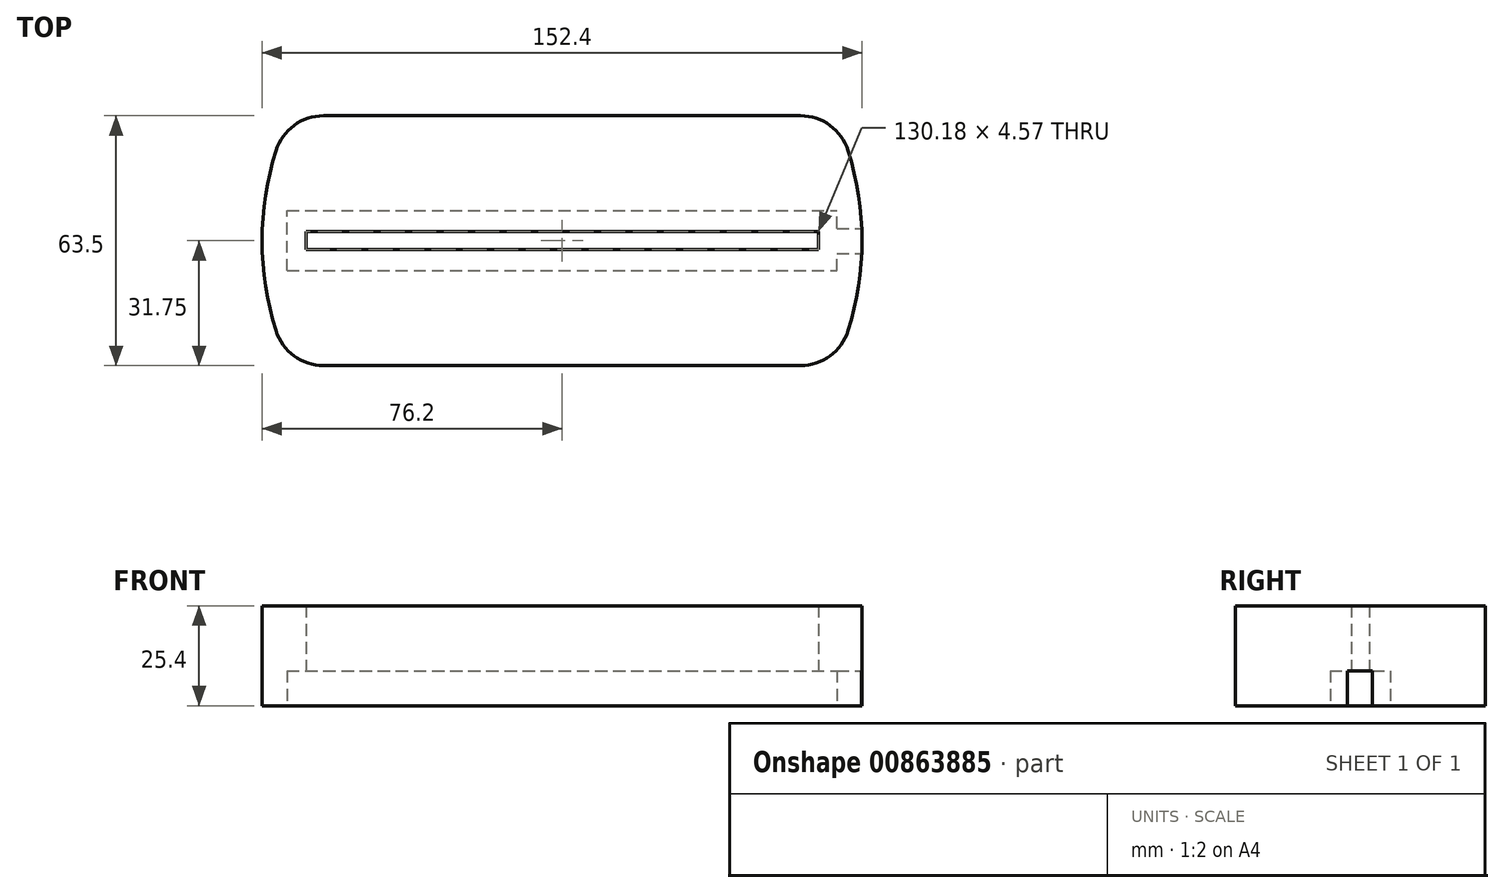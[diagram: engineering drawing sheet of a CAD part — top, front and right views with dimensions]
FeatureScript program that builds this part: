
annotation { "Feature Type Name" : "Feature", "Feature Type Description" : "" }
export const myFeature = defineFeature(function(context is Context, id is Id, definition is map)
    precondition{}
    {
        {
            var Q0;
            Q0=qCreatedBy(makeId("Top.planeOp"),FACE);
            var sketch = newSketch(context, id + "F0", { "sketchPlane" : qUnion([Q0])});
            skArc(sketch, "E0", {"start": v(-69.27, 31.75) * mm, "mid": v(-76.2, 0) * mm, "end": v(-69.27, -31.75) * mm});
            skLineSegment(sketch, "E1", {"start": v(-69.27, 31.75) * mm, "end": v(69.27, 31.75) * mm});
            skLineSegment(sketch, "E2.MirrorCS", {"start": v(-69.27, -31.75) * mm, "end": v(69.27, -31.75) * mm});
            skArc(sketch, "E3.trimOffspring", {"start": v(69.27, -31.75) * mm, "mid": v(76.2, 0) * mm, "end": v(69.27, 31.75) * mm});
            skSolve(sketch);
        }
        {
            var Q0;
            Q0=makeQuery(id+"F0.imprint","IMPRINT",FACE,{"disambiguationData":[TD([[makeQuery(id+"F0.imprint","IMPRINT",EDGE,{"derivedFrom":sQuery(id+"F0.wireOp",EDGE,"E0")}),1.0]])]});
            extrude(context, id + "F1", {"entities" : qUnion([Q0]), "depth" : 25.4 * mm, "offsetDistance" : 25.4 * mm});
        }
        {
            var Q0;
            Q0=makeQuery(id+"F1.opExtrude","CAP_FACE",FACE,{"disambiguationData":[OSD([sQuery(id+"F0.wireOp",EDGE,"E0"),sQuery(id+"F0.wireOp",EDGE,"E1"),sQuery(id+"F0.wireOp",EDGE,"E2.MirrorCS"),sQuery(id+"F0.wireOp",EDGE,"E3.trimOffspring")])],"isStart":true});
            var sketch = newSketch(context, id + "F2", { "sketchPlane" : qUnion([Q0])});
            skLineSegment(sketch, "E4.MirrorCS", {"start": v(-179.86, 3.34) * mm, "end": v(-179.86, -2.97) * mm});
            skLineSegment(sketch, "E5.bottom", {"start": v(-65.09, 2.29) * mm, "end": v(65.09, 2.29) * mm});
            skLineSegment(sketch, "E5.top", {"start": v(-65.09, -2.29) * mm, "end": v(65.09, -2.29) * mm});
            skLineSegment(sketch, "E5.left", {"start": v(-65.09, 2.29) * mm, "end": v(-65.09, -2.29) * mm});
            skLineSegment(sketch, "E5.right", {"start": v(65.09, 2.29) * mm, "end": v(65.09, -2.29) * mm});
            skPoint(sketch, "E5.middle", {"position": v(0, 0) * mm});
            skSolve(sketch);
        }
        {
            var Q0;
            Q0=makeQuery(id+"F2.imprint","IMPRINT",FACE,{"disambiguationData":[TD([[makeQuery(id+"F2.imprint","IMPRINT",EDGE,{"derivedFrom":sQuery(id+"F2.wireOp",EDGE,"E5.bottom")}),-1.0]])]});
            extrude(context, id + "F3", {"entities" : qUnion([Q0]), "operationType" : NewBodyOperationType.REMOVE, "endBound" : BoundingType.THROUGH_ALL, "oppositeDirection" : true, "depth" : 25.4 * mm, "offsetDistance" : 25.4 * mm});
        }
        {
            var Q0;
            Q0=makeQuery(id+"F1.opExtrude","CAP_FACE",FACE,{"disambiguationData":[OSD([sQuery(id+"F0.wireOp",EDGE,"E0"),sQuery(id+"F0.wireOp",EDGE,"E1"),sQuery(id+"F0.wireOp",EDGE,"E2.MirrorCS"),sQuery(id+"F0.wireOp",EDGE,"E3.trimOffspring")])],"isStart":true});
            var sketch = newSketch(context, id + "F4", { "sketchPlane" : qUnion([Q0])});
            skLineSegment(sketch, "E6.bottom", {"start": v(-69.85, 7.62) * mm, "end": v(69.85, 7.62) * mm});
            skLineSegment(sketch, "E6.top", {"start": v(-69.85, -7.62) * mm, "end": v(69.85, -7.62) * mm});
            skLineSegment(sketch, "E6.left", {"start": v(-69.85, 7.62) * mm, "end": v(-69.85, -7.62) * mm});
            skLineSegment(sketch, "E6.right", {"start": v(69.85, 7.62) * mm, "end": v(69.85, -7.62) * mm});
            skPoint(sketch, "E6.middle", {"position": v(0, 0) * mm});
            skLineSegment(sketch, "E7", {"start": v(69.85, 3.23) * mm, "end": v(76.13, 3.23) * mm});
            skLineSegment(sketch, "E8", {"start": v(69.85, -3.12) * mm, "end": v(76.14, -3.12) * mm});
            skArc(sketch, "E9", {"start": v(76.14, -3.12) * mm, "mid": v(76.2, 0.06) * mm, "end": v(76.13, 3.23) * mm});
            skSolve(sketch);
        }
        {
            var Q0;
            Q0=makeQuery(id+"F4.imprint","IMPRINT",FACE,{"disambiguationData":[TD([[makeQuery(id+"F4.imprint","IMPRINT",EDGE,{"derivedFrom":sQuery(id+"F4.wireOp",EDGE,"E6.bottom")}),-1.0]])]});
            var Q1;
            {var subQ0=sQuery(id+"F4.wireOp",EDGE,"E7");Q1=makeQuery(id+"F4.imprint","IMPRINT",FACE,{"disambiguationData":[TD([[makeQuery(id+"F4.imprint","IMPRINT",EDGE,{"derivedFrom":subQ0}),-1.0]])]});}
            extrude(context, id + "F5", {"entities" : qUnion([Q0, Q1]), "operationType" : NewBodyOperationType.REMOVE, "oppositeDirection" : true, "depth" : 8.9 * mm, "offsetDistance" : 25.4 * mm});
        }
        {
            var Q0;
            Q0=makeQuery(id+"F1.opExtrude","SWEPT_EDGE",EDGE,{"disambiguationData":[OSD([sQuery(id+"F0.wireOp",EDGE,"E2.MirrorCS"),sQuery(id+"F0.wireOp",EDGE,"E3.trimOffspring")])]});
            var Q1;
            Q1=makeQuery(id+"F1.opExtrude","SWEPT_EDGE",EDGE,{"disambiguationData":[OSD([sQuery(id+"F0.wireOp",EDGE,"E1"),sQuery(id+"F0.wireOp",EDGE,"E3.trimOffspring")])]});
            var Q2;
            Q2=makeQuery(id+"F1.opExtrude","SWEPT_EDGE",EDGE,{"disambiguationData":[OSD([sQuery(id+"F0.wireOp",EDGE,"E0"),sQuery(id+"F0.wireOp",EDGE,"E2.MirrorCS")])]});
            var Q3;
            Q3=makeQuery(id+"F1.opExtrude","SWEPT_EDGE",EDGE,{"disambiguationData":[OSD([sQuery(id+"F0.wireOp",EDGE,"E0"),sQuery(id+"F0.wireOp",EDGE,"E1")])]});
            fillet(context, id + "F6", {"entities" : qUnion([Q0, Q1, Q2, Q3]), "radius" : 12.7 * mm, "tangentPropagation" : true, "allowEdgeOverflow" : false});
        }
    });
